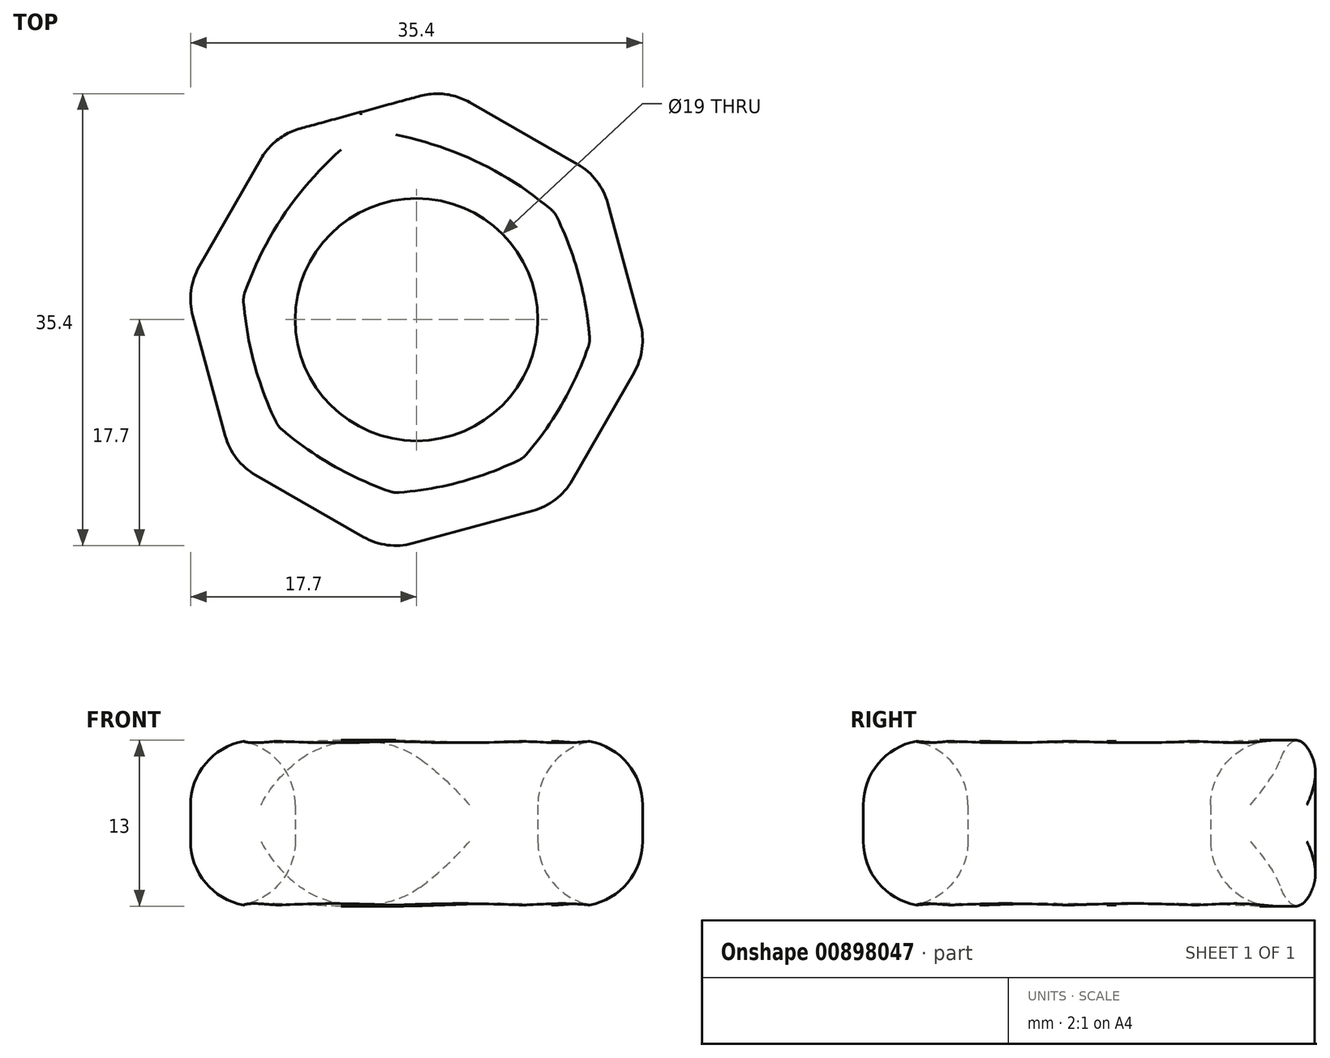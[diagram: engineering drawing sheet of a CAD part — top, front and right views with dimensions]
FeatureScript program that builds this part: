
annotation { "Feature Type Name" : "Feature", "Feature Type Description" : "" }
export const myFeature = defineFeature(function(context is Context, id is Id, definition is map)
    precondition{}
    {
        {
            var Q0;
            Q0=qCreatedBy(makeId("Top.planeOp"),FACE);
            var sketch = newSketch(context, id + "F0", { "sketchPlane" : qUnion([Q0])});
            skCircle(sketch, "E0.cCircle", {"center": v(0, 0) * mm, "radius": 16.84 * mm, "construction": true});
            skLineSegment(sketch, "E0.0", {"start": v(-18.08, 2.33) * mm, "end": v(-11.13, 14.43) * mm});
            skLineSegment(sketch, "E0.1", {"start": v(-11.13, 14.43) * mm, "end": v(2.33, 18.08) * mm});
            skLineSegment(sketch, "E0.2", {"start": v(2.33, 18.08) * mm, "end": v(14.43, 11.13) * mm});
            skLineSegment(sketch, "E0.3", {"start": v(14.43, 11.13) * mm, "end": v(18.08, -2.33) * mm});
            skLineSegment(sketch, "E0.4", {"start": v(18.08, -2.33) * mm, "end": v(11.13, -14.43) * mm});
            skLineSegment(sketch, "E0.5", {"start": v(11.13, -14.43) * mm, "end": v(-2.33, -18.08) * mm});
            skLineSegment(sketch, "E0.6", {"start": v(-2.33, -18.08) * mm, "end": v(-14.43, -11.13) * mm});
            skLineSegment(sketch, "E0.7", {"start": v(-14.43, -11.13) * mm, "end": v(-18.08, 2.33) * mm});
            skPoint(sketch, "E0.0.midPoint", {"position": v(-14.6, 8.38) * mm});
            skCircle(sketch, "E1", {"center": v(0, 0) * mm, "radius": 9.5 * mm});
            skSolve(sketch);
        }
        {
            var Q0;
            Q0 = qSketchRegion(id + "F0", true);
            extrude(context, id + "F1", {"entities" : qUnion([Q0]), "depth" : 13 * mm, "offsetDistance" : 25.4 * mm});
        }
        {
            var Q0;
            Q0=makeQuery(id+"F1.opExtrude","CAP_EDGE",EDGE,{"disambiguationData":[OSD([sQuery(id+"F0.wireOp",EDGE,"E1")])],"isStart":true});
            var Q1;
            Q1=makeQuery(id+"F1.opExtrude","CAP_EDGE",EDGE,{"disambiguationData":[OSD([sQuery(id+"F0.wireOp",EDGE,"E1")])],"isStart":false});
            var Q2;
            Q2=makeQuery(id+"F1.opExtrude","SWEPT_FACE",FACE,{"disambiguationData":[OSD([sQuery(id+"F0.wireOp",EDGE,"E0.2")])]});
            var Q3;
            Q3=makeQuery(id+"F1.opExtrude","SWEPT_FACE",FACE,{"disambiguationData":[OSD([sQuery(id+"F0.wireOp",EDGE,"E0.3")])]});
            var Q4;
            Q4=makeQuery(id+"F1.opExtrude","SWEPT_FACE",FACE,{"disambiguationData":[OSD([sQuery(id+"F0.wireOp",EDGE,"E0.4")])]});
            var Q5;
            Q5=makeQuery(id+"F1.opExtrude","SWEPT_FACE",FACE,{"disambiguationData":[OSD([sQuery(id+"F0.wireOp",EDGE,"E0.5")])]});
            var Q6;
            Q6=makeQuery(id+"F1.opExtrude","SWEPT_FACE",FACE,{"disambiguationData":[OSD([sQuery(id+"F0.wireOp",EDGE,"E0.6")])]});
            var Q7;
            Q7=makeQuery(id+"F1.opExtrude","SWEPT_FACE",FACE,{"disambiguationData":[OSD([sQuery(id+"F0.wireOp",EDGE,"E0.7")])]});
            var Q8;
            Q8=makeQuery(id+"F1.opExtrude","SWEPT_FACE",FACE,{"disambiguationData":[OSD([sQuery(id+"F0.wireOp",EDGE,"E0.0")])]});
            fillet(context, id + "F2", {"entities" : qUnion([Q0, Q1, Q2, Q3, Q4, Q5, Q6, Q7, Q8]), "radius" : 5.08 * mm, "tangentPropagation" : true, "allowEdgeOverflow" : false});
        }
    });
